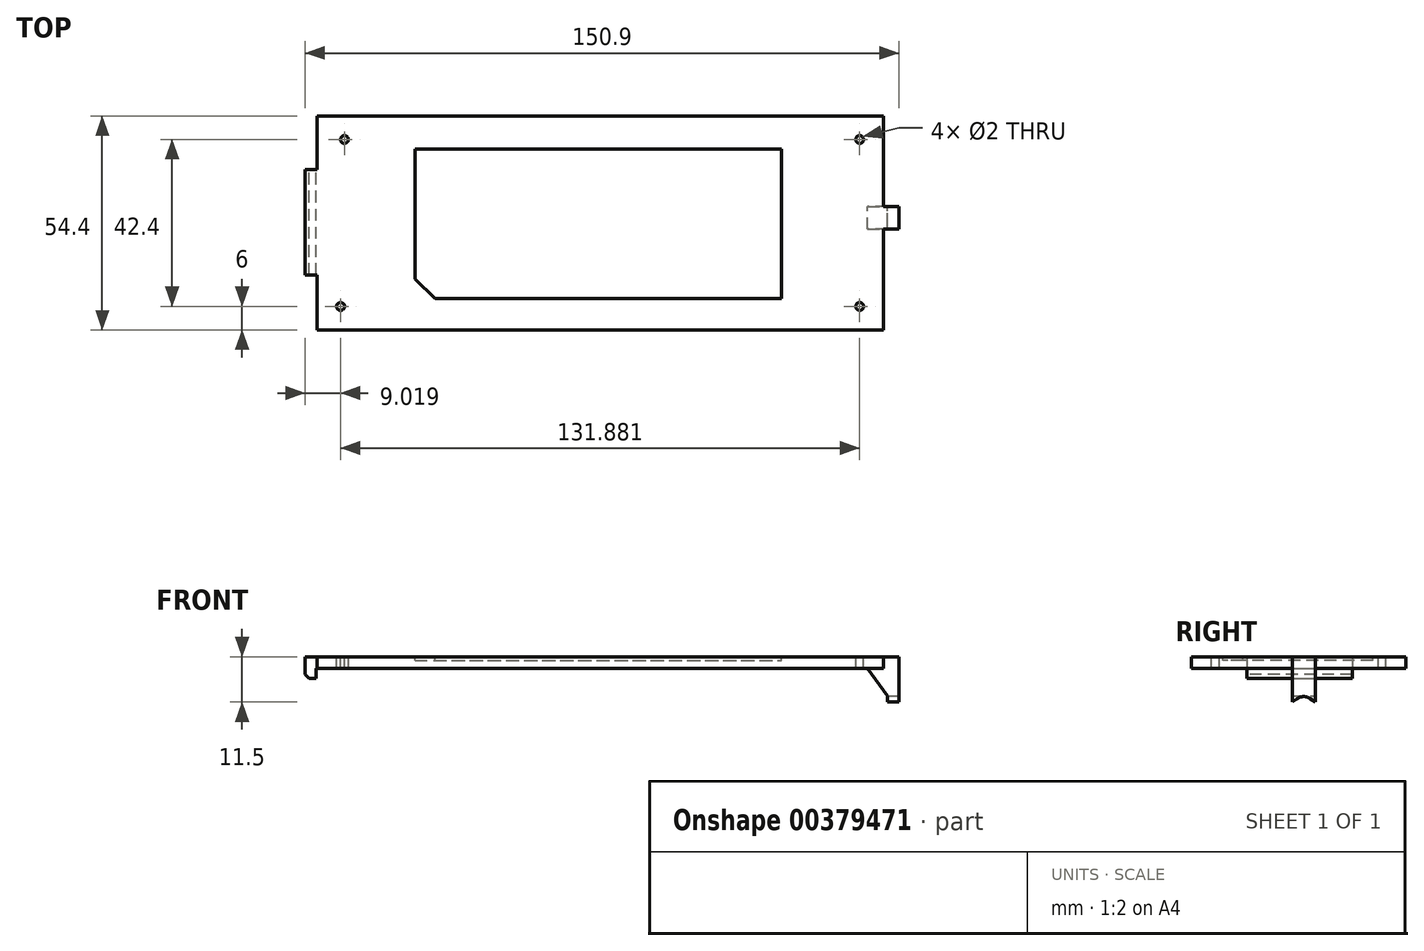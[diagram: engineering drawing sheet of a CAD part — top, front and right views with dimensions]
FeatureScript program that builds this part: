
annotation { "Feature Type Name" : "Feature", "Feature Type Description" : "" }
export const myFeature = defineFeature(function(context is Context, id is Id, definition is map)
    precondition{}
    {
        {
            var Q0;
            Q0=qCreatedBy(makeId("Top.planeOp"),FACE);
            var sketch = newSketch(context, id + "F0", { "sketchPlane" : qUnion([Q0])});
            skLineSegment(sketch, "E0.bottom", {"start": v(0, 0) * mm, "end": v(143.9, 0) * mm});
            skLineSegment(sketch, "E0.top", {"start": v(0, -54.4) * mm, "end": v(143.9, -54.4) * mm});
            skLineSegment(sketch, "E0.left", {"start": v(0, 0) * mm, "end": v(0, -54.4) * mm});
            skLineSegment(sketch, "E0.right", {"start": v(143.9, 0) * mm, "end": v(143.9, -54.4) * mm});
            skSolve(sketch);
        }
        {
            var Q0;
            Q0 = qSketchRegion(id + "F0", true);
            extrude(context, id + "F1", {"entities" : qUnion([Q0]), "depth" : 3 * mm});
        }
        {
            var Q0;
            Q0=makeQuery(id+"F1.opExtrude","SWEPT_FACE",FACE,{"disambiguationData":[OSD([sQuery(id+"F0.wireOp",EDGE,"E0.right")])]});
            var sketch = newSketch(context, id + "F2", { "sketchPlane" : qUnion([Q0])});
            skLineSegment(sketch, "E1.bottom", {"start": v(-28.8, 3) * mm, "end": v(-23, 3) * mm});
            skLineSegment(sketch, "E1.top", {"start": v(-28.8, 0) * mm, "end": v(-23, 0) * mm});
            skLineSegment(sketch, "E1.left", {"start": v(-28.8, 3) * mm, "end": v(-28.8, 0) * mm});
            skLineSegment(sketch, "E1.right", {"start": v(-23, 3) * mm, "end": v(-23, 0) * mm});
            skSolve(sketch);
        }
        {
            var Q0;
            Q0 = qSketchRegion(id + "F2", true);
            extrude(context, id + "F3", {"entities" : qUnion([Q0]), "operationType" : NewBodyOperationType.ADD, "depth" : 4 * mm});
        }
        {
            var Q0;
            Q0=makeQuery(id+"F3.boolean.opBoolean","MERGE",FACE,{"derivedFrom":[makeQuery(id+"F1.opExtrude","CAP_FACE",FACE,{"disambiguationData":[OSD([sQuery(id+"F0.wireOp",EDGE,"E0.bottom"),sQuery(id+"F0.wireOp",EDGE,"E0.top"),sQuery(id+"F0.wireOp",EDGE,"E0.left"),sQuery(id+"F0.wireOp",EDGE,"E0.right")])],"isStart":true}),makeQuery(id+"F3.opExtrude","SWEPT_FACE",FACE,{"disambiguationData":[OSD([sQuery(id+"F2.wireOp",EDGE,"E1.top")])]})]});
            var sketch = newSketch(context, id + "F4", { "sketchPlane" : qUnion([Q0])});
            skLineSegment(sketch, "E2.bottom", {"start": v(143.9, 28.8) * mm, "end": v(147.9, 28.8) * mm});
            skLineSegment(sketch, "E2.top", {"start": v(143.9, 23) * mm, "end": v(147.9, 23) * mm});
            skLineSegment(sketch, "E2.left", {"start": v(143.9, 28.8) * mm, "end": v(143.9, 23) * mm});
            skLineSegment(sketch, "E2.right", {"start": v(147.9, 28.8) * mm, "end": v(147.9, 23) * mm});
            skSolve(sketch);
        }
        {
            var Q0;
            Q0 = qSketchRegion(id + "F4", true);
            extrude(context, id + "F5", {"entities" : qUnion([Q0]), "operationType" : NewBodyOperationType.ADD, "depth" : 8.5 * mm});
        }
        {
            var Q0;
            Q0=makeQuery(id+"F5.boolean.opBoolean","MERGE",FACE,{"derivedFrom":[makeQuery(id+"F3.opExtrude","CAP_FACE",FACE,{"disambiguationData":[OSD([sQuery(id+"F2.wireOp",EDGE,"E1.bottom"),sQuery(id+"F2.wireOp",EDGE,"E1.top"),sQuery(id+"F2.wireOp",EDGE,"E1.left"),sQuery(id+"F2.wireOp",EDGE,"E1.right")])],"isStart":false}),makeQuery(id+"F5.opExtrude","SWEPT_FACE",FACE,{"disambiguationData":[OSD([sQuery(id+"F4.wireOp",EDGE,"E2.right")])]})]});
            var sketch = newSketch(context, id + "F6", { "sketchPlane" : qUnion([Q0])});
            skLineSegment(sketch, "E3", {"start": v(-28.8, -8.5) * mm, "end": v(-25.9, -6.47) * mm});
            skLineSegment(sketch, "E4", {"start": v(-25.9, -6.47) * mm, "end": v(-23, -8.5) * mm});
            skLineSegment(sketch, "E5", {"start": v(-28.8, -8.5) * mm, "end": v(-23, -8.5) * mm});
            skSolve(sketch);
        }
        {
            var Q0;
            Q0 = qSketchRegion(id + "F6", true);
            extrude(context, id + "F7", {"entities" : qUnion([Q0]), "operationType" : NewBodyOperationType.REMOVE, "oppositeDirection" : true, "depth" : 5 * mm});
        }
        {
            var Q0;
            Q0=makeQuery(id+"F7.boolean.opBoolean","COPY",EDGE,{"derivedFrom":makeQuery(id+"F7.opExtrude","SWEPT_EDGE",EDGE,{"disambiguationData":[OSD([sQuery(id+"F6.wireOp",EDGE,"E3"),sQuery(id+"F6.wireOp",EDGE,"E4")])]})});
            fillet(context, id + "F8", {"entities" : qUnion([Q0]), "radius" : 3 * mm, "tangentPropagation" : true, "allowEdgeOverflow" : false});
        }
        {
            var Q0;
            Q0=makeQuery(id+"F1.opExtrude","SWEPT_FACE",FACE,{"disambiguationData":[OSD([sQuery(id+"F0.wireOp",EDGE,"E0.left")])]});
            var sketch = newSketch(context, id + "F9", { "sketchPlane" : qUnion([Q0])});
            skLineSegment(sketch, "E6.bottom", {"start": v(13.6, 3) * mm, "end": v(40.4, 3) * mm});
            skLineSegment(sketch, "E6.top", {"start": v(13.6, 0) * mm, "end": v(40.4, 0) * mm});
            skLineSegment(sketch, "E6.left", {"start": v(13.6, 3) * mm, "end": v(13.6, 0) * mm});
            skLineSegment(sketch, "E6.right", {"start": v(40.4, 3) * mm, "end": v(40.4, 0) * mm});
            skSolve(sketch);
        }
        {
            var Q0;
            Q0 = qSketchRegion(id + "F9", true);
            extrude(context, id + "F10", {"entities" : qUnion([Q0]), "operationType" : NewBodyOperationType.ADD, "depth" : 3 * mm});
        }
        {
            var Q0;
            Q0=makeQuery(id+"F10.boolean.opBoolean","MERGE",FACE,{"derivedFrom":[makeQuery(id+"F3.boolean.opBoolean","MERGE",FACE,{"derivedFrom":[makeQuery(id+"F1.opExtrude","CAP_FACE",FACE,{"disambiguationData":[OSD([sQuery(id+"F0.wireOp",EDGE,"E0.bottom"),sQuery(id+"F0.wireOp",EDGE,"E0.top"),sQuery(id+"F0.wireOp",EDGE,"E0.left"),sQuery(id+"F0.wireOp",EDGE,"E0.right")])],"isStart":true}),makeQuery(id+"F3.opExtrude","SWEPT_FACE",FACE,{"disambiguationData":[OSD([sQuery(id+"F2.wireOp",EDGE,"E1.top")])]})]}),makeQuery(id+"F10.opExtrude","SWEPT_FACE",FACE,{"disambiguationData":[OSD([sQuery(id+"F9.wireOp",EDGE,"E6.top")])]})]});
            var sketch = newSketch(context, id + "F11", { "sketchPlane" : qUnion([Q0])});
            skLineSegment(sketch, "E7.bottom", {"start": v(-3, 40.4) * mm, "end": v(0, 40.4) * mm});
            skLineSegment(sketch, "E7.top", {"start": v(-3, 13.6) * mm, "end": v(0, 13.6) * mm});
            skLineSegment(sketch, "E7.left", {"start": v(-3, 40.4) * mm, "end": v(-3, 13.6) * mm});
            skLineSegment(sketch, "E7.right", {"start": v(0, 40.4) * mm, "end": v(0, 13.6) * mm});
            skSolve(sketch);
        }
        {
            var Q0;
            Q0 = qSketchRegion(id + "F11", true);
            extrude(context, id + "F12", {"entities" : qUnion([Q0]), "operationType" : NewBodyOperationType.ADD, "depth" : 2.5 * mm});
        }
        {
            var Q0;
            Q0=makeQuery(id+"F12.opExtrude","SWEPT_FACE",FACE,{"disambiguationData":[OSD([sQuery(id+"F11.wireOp",EDGE,"E7.right")])]});
            var sketch = newSketch(context, id + "F13", { "sketchPlane" : qUnion([Q0])});
            skLineSegment(sketch, "E8.bottom", {"start": v(-13.6, -2.5) * mm, "end": v(-40.4, -2.5) * mm});
            skLineSegment(sketch, "E8.top", {"start": v(-13.6, 0) * mm, "end": v(-40.4, 0) * mm});
            skLineSegment(sketch, "E8.left", {"start": v(-13.6, -2.5) * mm, "end": v(-13.6, 0) * mm});
            skLineSegment(sketch, "E8.right", {"start": v(-40.4, -2.5) * mm, "end": v(-40.4, 0) * mm});
            skSolve(sketch);
        }
        {
            var Q0;
            Q0 = qSketchRegion(id + "F13", true);
            extrude(context, id + "F14", {"entities" : qUnion([Q0]), "operationType" : NewBodyOperationType.REMOVE, "oppositeDirection" : true, "depth" : 0.2 * mm});
        }
        {
            var Q0;
            Q0=makeQuery(id+"F10.boolean.opBoolean","MERGE",FACE,{"derivedFrom":[makeQuery(id+"F3.boolean.opBoolean","MERGE",FACE,{"derivedFrom":[makeQuery(id+"F1.opExtrude","CAP_FACE",FACE,{"disambiguationData":[OSD([sQuery(id+"F0.wireOp",EDGE,"E0.bottom"),sQuery(id+"F0.wireOp",EDGE,"E0.top"),sQuery(id+"F0.wireOp",EDGE,"E0.left"),sQuery(id+"F0.wireOp",EDGE,"E0.right")])],"isStart":false}),makeQuery(id+"F3.opExtrude","SWEPT_FACE",FACE,{"disambiguationData":[OSD([sQuery(id+"F2.wireOp",EDGE,"E1.bottom")])]})]}),makeQuery(id+"F10.opExtrude","SWEPT_FACE",FACE,{"disambiguationData":[OSD([sQuery(id+"F9.wireOp",EDGE,"E6.bottom")])]})]});
            var sketch = newSketch(context, id + "F15", { "sketchPlane" : qUnion([Q0])});
            skLineSegment(sketch, "E9.bottom", {"start": v(25, -8.4) * mm, "end": v(118, -8.4) * mm});
            skLineSegment(sketch, "E9.top", {"start": v(30, -46.4) * mm, "end": v(118, -46.4) * mm});
            skLineSegment(sketch, "E9.left", {"start": v(25, -8.4) * mm, "end": v(25, -41.4) * mm});
            skLineSegment(sketch, "E9.right", {"start": v(118, -8.4) * mm, "end": v(118, -46.4) * mm});
            skLineSegment(sketch, "E10", {"start": v(25, -41.4) * mm, "end": v(30, -46.4) * mm});
            skSolve(sketch);
        }
        {
            var Q0;
            Q0 = qSketchRegion(id + "F15", true);
            extrude(context, id + "F16", {"entities" : qUnion([Q0]), "operationType" : NewBodyOperationType.REMOVE, "oppositeDirection" : true, "depth" : 1 * mm});
        }
        {
            var Q0;
            Q0=makeQuery(id+"F5.opExtrude","SWEPT_FACE",FACE,{"disambiguationData":[OSD([sQuery(id+"F4.wireOp",EDGE,"E2.left")])]});
            var sketch = newSketch(context, id + "F17", { "sketchPlane" : qUnion([Q0])});
            skLineSegment(sketch, "E11.bottom", {"start": v(23, 0) * mm, "end": v(28.8, 0) * mm});
            skLineSegment(sketch, "E11.top", {"start": v(23, -12.27) * mm, "end": v(28.8, -12.27) * mm});
            skLineSegment(sketch, "E11.left", {"start": v(23, 0) * mm, "end": v(23, -12.27) * mm});
            skLineSegment(sketch, "E11.right", {"start": v(28.8, 0) * mm, "end": v(28.8, -12.27) * mm});
            skSolve(sketch);
        }
        {
            var Q0;
            Q0 = qSketchRegion(id + "F17", true);
            extrude(context, id + "F18", {"entities" : qUnion([Q0]), "operationType" : NewBodyOperationType.REMOVE, "oppositeDirection" : true, "depth" : 1 * mm});
        }
        {
            var Q0;
            Q0=makeQuery(id+"F5.boolean.opBoolean","MERGE",FACE,{"derivedFrom":[makeQuery(id+"F3.opExtrude","SWEPT_FACE",FACE,{"disambiguationData":[OSD([sQuery(id+"F2.wireOp",EDGE,"E1.right")])]}),makeQuery(id+"F5.opExtrude","SWEPT_FACE",FACE,{"disambiguationData":[OSD([sQuery(id+"F4.wireOp",EDGE,"E2.top")])]})]});
            var sketch = newSketch(context, id + "F19", { "sketchPlane" : qUnion([Q0])});
            skLineSegment(sketch, "E12", {"start": v(-144.9, 0) * mm, "end": v(-144.9, -7) * mm});
            skLineSegment(sketch, "E13", {"start": v(-144.9, -7) * mm, "end": v(-139.9, 0) * mm});
            skLineSegment(sketch, "E14", {"start": v(-139.9, 0) * mm, "end": v(-144.9, 0) * mm});
            skSolve(sketch);
        }
        {
            var Q0;
            Q0 = qSketchRegion(id + "F19", true);
            extrude(context, id + "F20", {"entities" : qUnion([Q0]), "operationType" : NewBodyOperationType.ADD, "oppositeDirection" : true, "depth" : 5.8 * mm});
        }
        {
            var Q0;
            Q0=makeQuery(id+"F12.opExtrude","CAP_EDGE",EDGE,{"disambiguationData":[OSD([sQuery(id+"F11.wireOp",EDGE,"E7.left")])],"isStart":false});
            chamfer(context, id + "F21", {"entities" : qUnion([Q0]), "width" : 1 * mm, "tangentPropagation" : true});
        }
        {
            var Q0;
            Q0=makeQuery(id+"F10.boolean.opBoolean","MERGE",FACE,{"derivedFrom":[makeQuery(id+"F3.boolean.opBoolean","MERGE",FACE,{"derivedFrom":[makeQuery(id+"F1.opExtrude","CAP_FACE",FACE,{"disambiguationData":[OSD([sQuery(id+"F0.wireOp",EDGE,"E0.bottom"),sQuery(id+"F0.wireOp",EDGE,"E0.top"),sQuery(id+"F0.wireOp",EDGE,"E0.left"),sQuery(id+"F0.wireOp",EDGE,"E0.right")])],"isStart":false}),makeQuery(id+"F3.opExtrude","SWEPT_FACE",FACE,{"disambiguationData":[OSD([sQuery(id+"F2.wireOp",EDGE,"E1.bottom")])]})]}),makeQuery(id+"F10.opExtrude","SWEPT_FACE",FACE,{"disambiguationData":[OSD([sQuery(id+"F9.wireOp",EDGE,"E6.bottom")])]})]});
            var sketch = newSketch(context, id + "F22", { "sketchPlane" : qUnion([Q0])});
            skCircle(sketch, "E15", {"center": v(137.9, -48.4) * mm, "radius": 1 * mm});
            skCircle(sketch, "E16", {"center": v(137.9, -6) * mm, "radius": 1 * mm});
            skCircle(sketch, "E17", {"center": v(6.02, -48.4) * mm, "radius": 1 * mm});
            skCircle(sketch, "E18", {"center": v(7, -6) * mm, "radius": 1 * mm});
            skSolve(sketch);
        }
        {
            var Q0;
            Q0 = qSketchRegion(id + "F22", true);
            extrude(context, id + "F23", {"entities" : qUnion([Q0]), "operationType" : NewBodyOperationType.REMOVE, "oppositeDirection" : true, "depth" : 3 * mm});
        }
    });
